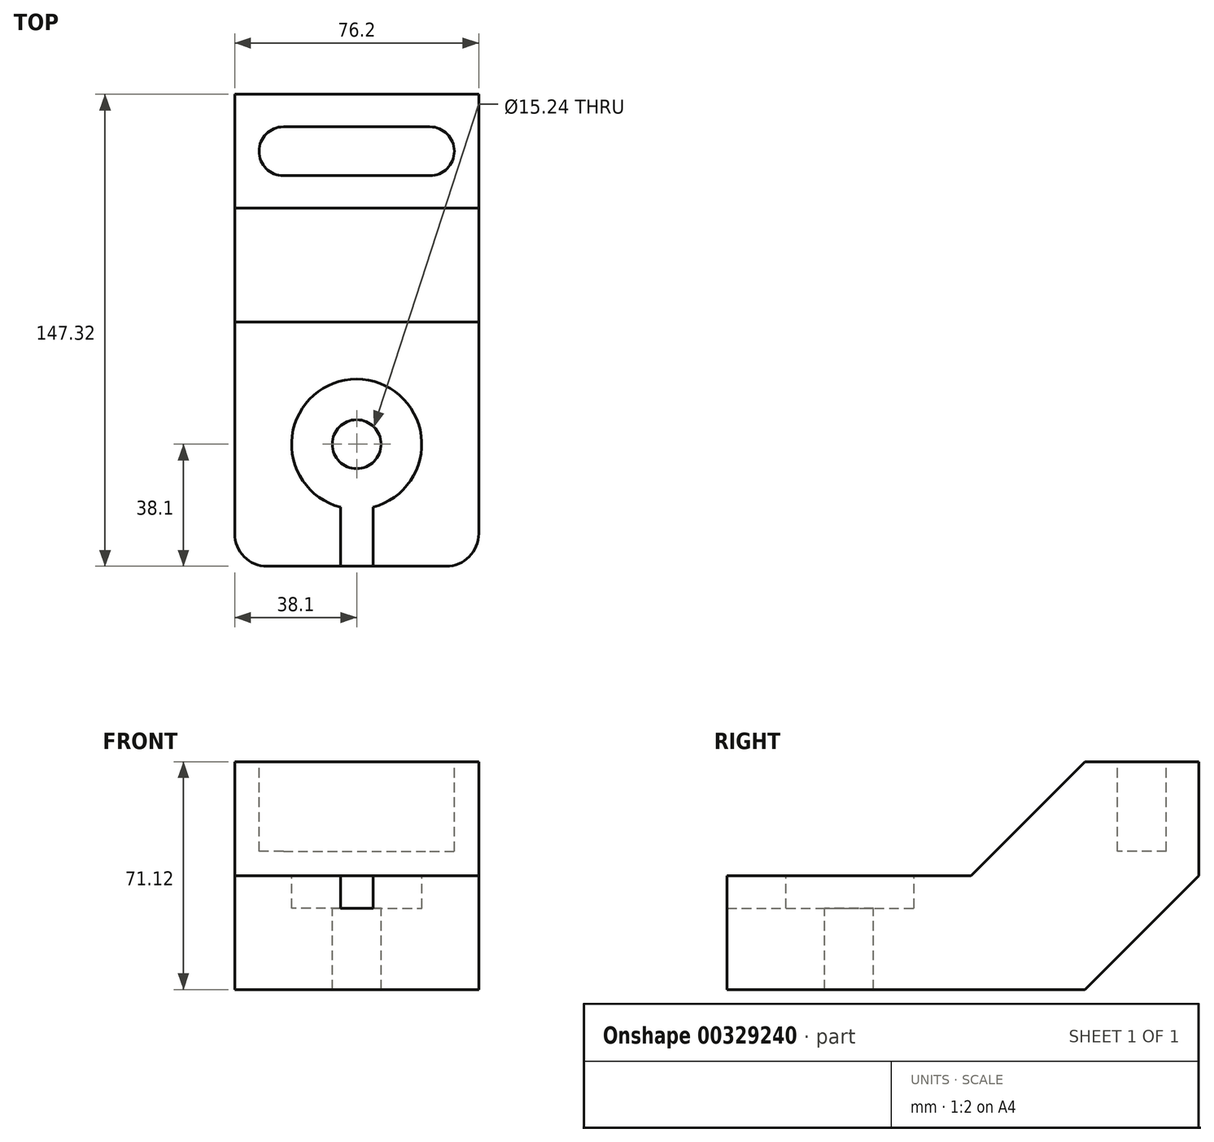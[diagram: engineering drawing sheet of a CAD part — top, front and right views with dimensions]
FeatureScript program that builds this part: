
annotation { "Feature Type Name" : "Feature", "Feature Type Description" : "" }
export const myFeature = defineFeature(function(context is Context, id is Id, definition is map)
    precondition{}
    {
        {
            var Q0;
            Q0=qCreatedBy(makeId("Top.planeOp"),FACE);
            var sketch = newSketch(context, id + "F0", { "sketchPlane" : qUnion([Q0])});
            skLineSegment(sketch, "E0", {"start": v(0, 0) * mm, "end": v(76.2, 0) * mm});
            skLineSegment(sketch, "E1", {"start": v(76.2, 0) * mm, "end": v(76.2, 76.2) * mm});
            skLineSegment(sketch, "E2", {"start": v(76.2, 76.2) * mm, "end": v(0, 76.2) * mm});
            skLineSegment(sketch, "E3", {"start": v(0, 76.2) * mm, "end": v(0, 0) * mm});
            skLineSegment(sketch, "E4", {"start": v(0, 76.2) * mm, "end": v(0, 147.32) * mm});
            skLineSegment(sketch, "E5", {"start": v(0, 147.32) * mm, "end": v(76.2, 147.32) * mm});
            skLineSegment(sketch, "E6", {"start": v(76.2, 147.32) * mm, "end": v(76.2, 76.2) * mm});
            skLineSegment(sketch, "E7", {"start": v(0, 111.76) * mm, "end": v(76.2, 111.76) * mm});
            skPoint(sketch, "E8", {"position": v(38.1, 38.1) * mm});
            skSolve(sketch);
        }
        {
            var Q0;
            {var subQ0=sQuery(id+"F0.wireOp",EDGE,"E5");Q0=makeQuery(id+"F0.imprint","IMPRINT",FACE,{"disambiguationData":[TD([[makeQuery(id+"F0.imprint","IMPRINT",EDGE,{"derivedFrom":subQ0}),-1.0]])]});}
            var Q1;
            {var subQ0=sQuery(id+"F0.wireOp",EDGE,"E2");Q1=makeQuery(id+"F0.imprint","IMPRINT",FACE,{"disambiguationData":[TD([[makeQuery(id+"F0.imprint","IMPRINT",EDGE,{"derivedFrom":subQ0}),-1.0]])]});}
            extrude(context, id + "F1", {"entities" : qUnion([Q0, Q1]), "depth" : 71.12 * mm});
        }
        {
            var Q0;
            Q0=makeQuery(id+"F0.imprint","IMPRINT",FACE,{"disambiguationData":[TD([[makeQuery(id+"F0.imprint","IMPRINT",EDGE,{"derivedFrom":sQuery(id+"F0.wireOp",EDGE,"E0")}),1.0]])]});
            extrude(context, id + "F2", {"entities" : qUnion([Q0]), "operationType" : NewBodyOperationType.ADD, "depth" : 35.56 * mm});
        }
        {
            var Q0;
            Q0=makeQuery(id+"F2.boolean.opBoolean","MERGE",FACE,{"derivedFrom":[makeQuery(id+"F1.opExtrude","SWEPT_FACE",FACE,{"disambiguationData":[OSD([sQuery(id+"F0.wireOp",EDGE,"E6")])]}),makeQuery(id+"F2.opExtrude","SWEPT_FACE",FACE,{"disambiguationData":[OSD([sQuery(id+"F0.wireOp",EDGE,"E1")])]})]});
            var sketch = newSketch(context, id + "F3", { "sketchPlane" : qUnion([Q0])});
            skLineSegment(sketch, "E9", {"start": v(76.2, 35.56) * mm, "end": v(76.2, 71.12) * mm});
            skLineSegment(sketch, "E10", {"start": v(76.2, 71.12) * mm, "end": v(111.76, 71.12) * mm});
            skLineSegment(sketch, "E11", {"start": v(111.76, 71.12) * mm, "end": v(76.2, 35.56) * mm});
            skLineSegment(sketch, "E12", {"start": v(147.32, 0) * mm, "end": v(147.32, 35.56) * mm});
            skLineSegment(sketch, "E13", {"start": v(147.32, 0) * mm, "end": v(111.76, 0) * mm});
            skLineSegment(sketch, "E14", {"start": v(111.76, 0) * mm, "end": v(147.32, 35.56) * mm});
            skSolve(sketch);
        }
        {
            var Q0;
            Q0=makeQuery(id+"F3.imprint","IMPRINT",FACE,{"disambiguationData":[TD([[makeQuery(id+"F3.imprint","IMPRINT",EDGE,{"derivedFrom":sQuery(id+"F3.wireOp",EDGE,"E9")}),1.0]])]});
            var Q1;
            Q1=makeQuery(id+"F3.imprint","IMPRINT",FACE,{"disambiguationData":[TD([[makeQuery(id+"F3.imprint","IMPRINT",EDGE,{"derivedFrom":sQuery(id+"F3.wireOp",EDGE,"E12")}),-1.0]])]});
            extrude(context, id + "F4", {"entities" : qUnion([Q0, Q1]), "operationType" : NewBodyOperationType.REMOVE, "oppositeDirection" : true, "depth" : 76.2 * mm});
        }
        {
            var Q0;
            Q0=makeQuery(id+"F2.opExtrude","CAP_FACE",FACE,{"disambiguationData":[OSD([sQuery(id+"F0.wireOp",EDGE,"E0"),sQuery(id+"F0.wireOp",EDGE,"E1"),sQuery(id+"F0.wireOp",EDGE,"E2"),sQuery(id+"F0.wireOp",EDGE,"E3")])],"isStart":false});
            var sketch = newSketch(context, id + "F5", { "sketchPlane" : qUnion([Q0])});
            skPoint(sketch, "E15", {"position": v(38.1, 38.1) * mm});
            skSolve(sketch);
        }
        {
            var Q0;
            Q0=sQuery(id+"F5.wireOp",VERTEX,"E15");
            var Q1;
            Q1=makeQuery(id+"F1.opExtrude","SWEPT_BODY",BODY,{"disambiguationData":[OSD([sQuery(id+"F0.wireOp",EDGE,"E2"),sQuery(id+"F0.wireOp",EDGE,"E4"),sQuery(id+"F0.wireOp",EDGE,"E5"),sQuery(id+"F0.wireOp",EDGE,"E6")])]});
            hole(context, id + "F6", {"style" : HoleStyle.C_BORE, "endStyle" : HoleEndStyle.THROUGH, "holeDiameter" : 15.24 * mm, "cBoreDiameter" : 40.64 * mm, "cBoreDepth" : 10.16 * mm, "tappedDepth" : 12.7 * mm, "tapClearance" : 3, "locations" : qUnion([Q0]), "scope" : qUnion([Q1])});
        }
        {
            var Q0;
            Q0=makeQuery(id+"F1.opExtrude","CAP_FACE",FACE,{"disambiguationData":[OSD([sQuery(id+"F0.wireOp",EDGE,"E2"),sQuery(id+"F0.wireOp",EDGE,"E4"),sQuery(id+"F0.wireOp",EDGE,"E5"),sQuery(id+"F0.wireOp",EDGE,"E6")])],"isStart":false});
            var sketch = newSketch(context, id + "F7", { "sketchPlane" : qUnion([Q0])});
            skPoint(sketch, "E16", {"position": v(15.24, 129.54) * mm});
            skPoint(sketch, "E17", {"position": v(60.96, 129.54) * mm});
            skArc(sketch, "E18", {"start": v(15.24, 137.16) * mm, "mid": v(7.62, 129.54) * mm, "end": v(15.24, 121.92) * mm});
            skLineSegment(sketch, "E19", {"start": v(15.24, 137.16) * mm, "end": v(60.96, 137.16) * mm});
            skLineSegment(sketch, "E20", {"start": v(15.24, 121.92) * mm, "end": v(60.96, 121.92) * mm});
            skArc(sketch, "E21", {"start": v(60.96, 121.92) * mm, "mid": v(68.58, 129.54) * mm, "end": v(60.96, 137.16) * mm});
            skSolve(sketch);
        }
        {
            var Q0;
            Q0=makeQuery(id+"F7.imprint","IMPRINT",FACE,{"disambiguationData":[TD([[makeQuery(id+"F7.imprint","IMPRINT",EDGE,{"derivedFrom":sQuery(id+"F7.wireOp",EDGE,"E18")}),1.0]])]});
            extrude(context, id + "F8", {"entities" : qUnion([Q0]), "operationType" : NewBodyOperationType.REMOVE, "oppositeDirection" : true, "depth" : 27.94 * mm});
        }
        {
            var Q0;
            Q0=makeQuery(id+"F2.opExtrude","CAP_FACE",FACE,{"disambiguationData":[OSD([sQuery(id+"F0.wireOp",EDGE,"E0"),sQuery(id+"F0.wireOp",EDGE,"E1"),sQuery(id+"F0.wireOp",EDGE,"E2"),sQuery(id+"F0.wireOp",EDGE,"E3")])],"isStart":false});
            var sketch = newSketch(context, id + "F9", { "sketchPlane" : qUnion([Q0])});
            skLineSegment(sketch, "E22", {"start": v(33.02, 76.2) * mm, "end": v(33.02, 0) * mm});
            skLineSegment(sketch, "E23", {"start": v(43.18, 0) * mm, "end": v(43.18, 76.2) * mm});
            skSolve(sketch);
        }
        {
            var Q0;
            {var subQ0=sQuery(id+"F9.wireOp",EDGE,"E22");var subQ1=makeQuery(id+"F2.opExtrude","CAP_EDGE",EDGE,{"disambiguationData":[OSD([sQuery(id+"F0.wireOp",EDGE,"E0")])],"isStart":false});var subQ2=makeQuery(id+"F9.imprint","INTERSECT",VERTEX,{"derivedFrom":[subQ1,subQ0]});Q0=makeQuery(id+"F9.imprint","IMPRINT",FACE,{"disambiguationData":[TD([[makeQuery(id+"F9.imprint","IMPRINT",EDGE,{"disambiguationData":[TD([[subQ2,-1.0]])],"derivedFrom":subQ1}),1.0]])]});}
            var Q1;
            {var subQ0=sQuery(id+"F9.wireOp",EDGE,"E22");var subQ1=makeQuery(id+"F6.hole-0.boolean.opBoolean","COPY",EDGE,{"derivedFrom":makeQuery(id+"F6.hole-0.opRevolve","SWEPT_EDGE",EDGE,{"disambiguationData":[OSD([sQuery(id+"F6.hole-0.sketch.wireOp",EDGE,"cbore_start_line_2"),sQuery(id+"F6.hole-0.sketch.wireOp",EDGE,"cbore_start_line_3")])]})});var subQ2=makeQuery(id+"F9.imprint","INTERSECT",VERTEX,{"disambiguationData":[OD(0.0)],"derivedFrom":[subQ1,subQ0]});Q1=makeQuery(id+"F9.imprint","IMPRINT",FACE,{"disambiguationData":[TD([[makeQuery(id+"F9.imprint","IMPRINT",EDGE,{"disambiguationData":[TD([[subQ2,-1.0]])],"derivedFrom":subQ0}),1.0]])]});}
            var Q2;
            {var subQ0=sQuery(id+"F9.wireOp",EDGE,"E22");var subQ3=makeQuery(id+"F6.hole-0.boolean.opBoolean","COPY",EDGE,{"derivedFrom":makeQuery(id+"F6.hole-0.opRevolve","SWEPT_EDGE",EDGE,{"disambiguationData":[OSD([sQuery(id+"F6.hole-0.sketch.wireOp",EDGE,"cbore_start_line_2"),sQuery(id+"F6.hole-0.sketch.wireOp",EDGE,"cbore_start_line_3")])]})});var subQ4=makeQuery(id+"F9.imprint","INTERSECT",VERTEX,{"disambiguationData":[OD(0.0)],"derivedFrom":[subQ3,subQ0]});Q2=makeQuery(id+"F9.imprint","IMPRINT",FACE,{"disambiguationData":[TD([[makeQuery(id+"F9.imprint","IMPRINT",EDGE,{"disambiguationData":[TD([[subQ4,1.0]])],"derivedFrom":subQ3}),-1.0]])]});}
            extrude(context, id + "F10", {"entities" : qUnion([Q0, Q1, Q2]), "operationType" : NewBodyOperationType.REMOVE, "oppositeDirection" : true, "depth" : 10.16 * mm});
        }
        {
            var Q0;
            Q0=makeQuery(id+"F2.opExtrude","SWEPT_EDGE",EDGE,{"disambiguationData":[OSD([sQuery(id+"F0.wireOp",EDGE,"E0"),sQuery(id+"F0.wireOp",EDGE,"E1")])]});
            var Q1;
            Q1=makeQuery(id+"F2.opExtrude","SWEPT_EDGE",EDGE,{"disambiguationData":[OSD([sQuery(id+"F0.wireOp",EDGE,"E0"),sQuery(id+"F0.wireOp",EDGE,"E3")])]});
            fillet(context, id + "F11", {"entities" : qUnion([Q0, Q1]), "radius" : 10.16 * mm, "tangentPropagation" : true, "allowEdgeOverflow" : false});
        }
    });
